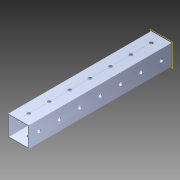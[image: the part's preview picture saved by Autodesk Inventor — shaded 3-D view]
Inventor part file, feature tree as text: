
AUTODESK INVENTOR PART (.ipt)
format: ipt  version: 2014 (Build 180170000, 170)  size: 1,164,800 bytes
history: native  units: in
note: dims shown in document units (in); Inventor stores cm internally (conversion verified against a paired STEP export)
features: pattern_circular x1, other x1, plane x1, extrude x1, imported_body x1, sketch x1
ambient origin geometry x8: Origin, YZ Plane, XZ Plane, XY Plane, X Axis, Y Axis, Z Axis, Center Point
bodies: Body1 (feature_tree)
feature tree (6):
  pattern_circular  "CirPattern2"
  other  "217-3426-STEP1"
  plane  "Work Plane1"
  extrude  "Extrusion1"  Depth=3937.0079in TaperAngle=0.0deg
  imported_body  "Base1"
  sketch  "Sketch1"  dims[d0=-7.0in d1=3937.0079in d2=0.0in]
